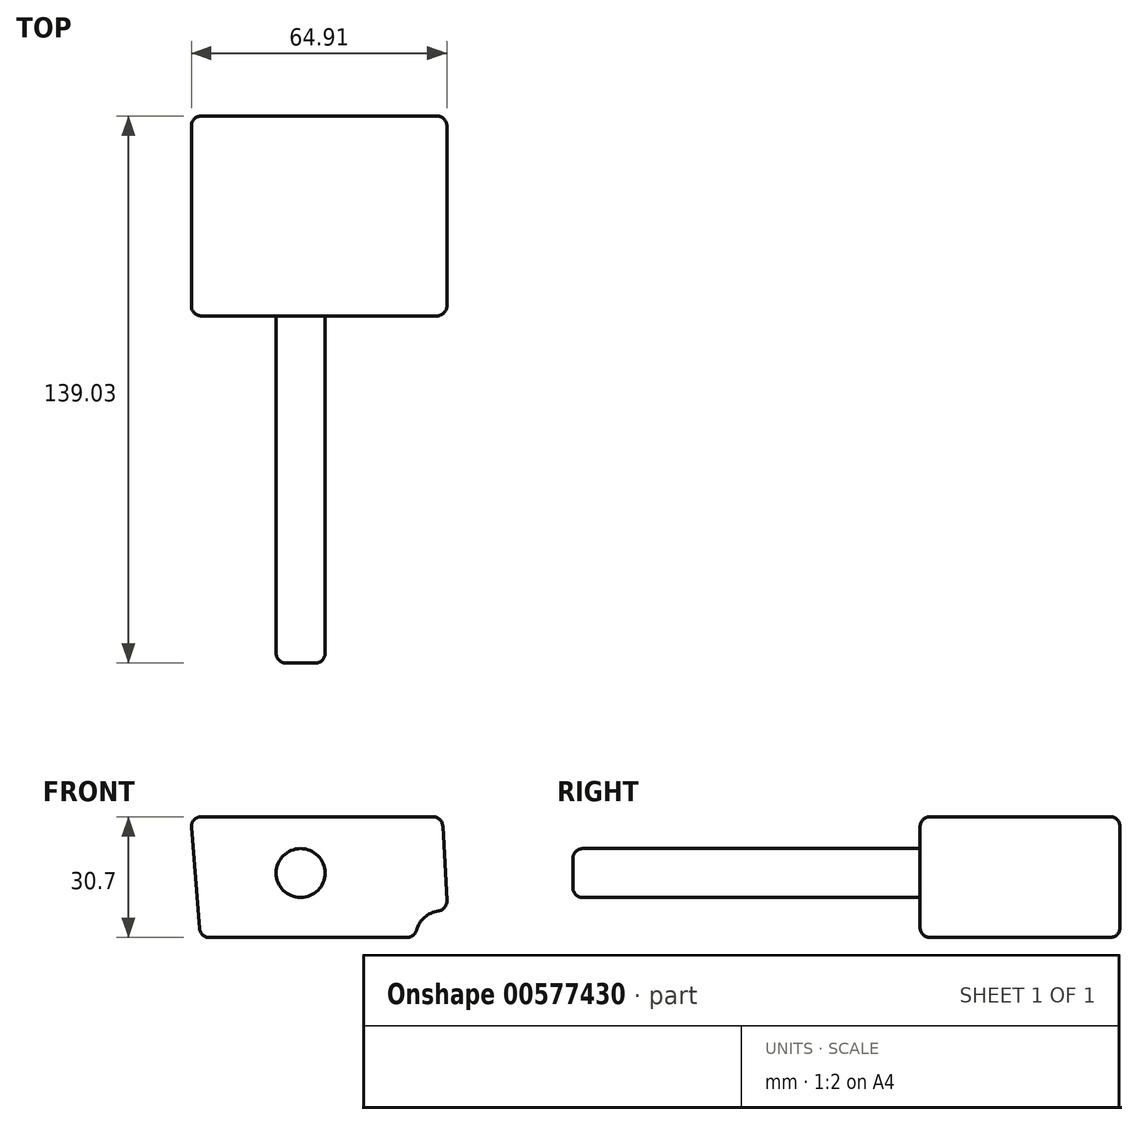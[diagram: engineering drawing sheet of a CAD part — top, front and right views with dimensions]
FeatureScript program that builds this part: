
annotation { "Feature Type Name" : "Feature", "Feature Type Description" : "" }
export const myFeature = defineFeature(function(context is Context, id is Id, definition is map)
    precondition{}
    {
        {
            var Q0;
            Q0=qCreatedBy(makeId("Front.planeOp"),FACE);
            var sketch = newSketch(context, id + "F0", { "sketchPlane" : qUnion([Q0])});
            skLineSegment(sketch, "E0", {"start": v(0, 0) * mm, "end": v(-63.97, 0) * mm});
            skLineSegment(sketch, "E1", {"start": v(-63.97, 0) * mm, "end": v(-61.53, -30.7) * mm});
            skLineSegment(sketch, "E2", {"start": v(-61.53, -30.7) * mm, "end": v(-6.83, -30.7) * mm});
            skLineSegment(sketch, "E3", {"start": v(1.3, -24) * mm, "end": v(0, 0) * mm});
            skArc(sketch, "E4", {"start": v(1.3, -24) * mm, "mid": v(-4.35, -25.44) * mm, "end": v(-6.83, -30.7) * mm});
            skSolve(sketch);
        }
        {
            var Q0;
            Q0=makeQuery(id+"F0.imprint","IMPRINT",FACE,{"disambiguationData":[TD([[makeQuery(id+"F0.imprint","IMPRINT",EDGE,{"derivedFrom":sQuery(id+"F0.wireOp",EDGE,"E0")}),1.0]])]});
            extrude(context, id + "F1", {"entities" : qUnion([Q0]), "depth" : 50.8 * mm, "offsetDistance" : 25.4 * mm});
        }
        {
            var Q0;
            Q0=makeQuery(id+"F1.opExtrude","CAP_FACE",FACE,{"disambiguationData":[OSD([sQuery(id+"F0.wireOp",EDGE,"E0"),sQuery(id+"F0.wireOp",EDGE,"E1"),sQuery(id+"F0.wireOp",EDGE,"E2"),sQuery(id+"F0.wireOp",EDGE,"9686c144-42a7-4e15-a98d-a6f16b45faf9"),sQuery(id+"F0.wireOp",EDGE,"E3")])],"isStart":false});
            var sketch = newSketch(context, id + "F2", { "sketchPlane" : qUnion([Q0])});
            skCircle(sketch, "E5", {"center": v(-36, -14.32) * mm, "radius": 6.22 * mm});
            skSolve(sketch);
        }
        {
            var Q0;
            Q0 = qSketchRegion(id + "F2", true);
            extrude(context, id + "F3", {"entities" : qUnion([Q0]), "operationType" : NewBodyOperationType.ADD, "endBound" : BoundingType.THROUGH_ALL, "depth" : 25.4 * mm, "offsetDistance" : 25.4 * mm});
        }
        {
            var Q0;
            Q0=makeQuery(id+"F3.opExtrude","CAP_EDGE",EDGE,{"disambiguationData":[OSD([sQuery(id+"F2.wireOp",EDGE,"E5")])],"isStart":false});
            var Q1;
            Q1=makeQuery(id+"F1.opExtrude","SWEPT_EDGE",EDGE,{"disambiguationData":[OSD([sQuery(id+"F0.wireOp",EDGE,"E1"),sQuery(id+"F0.wireOp",EDGE,"E2")])]});
            var Q2;
            Q2=makeQuery(id+"F1.opExtrude","SWEPT_EDGE",EDGE,{"disambiguationData":[OSD([sQuery(id+"F0.wireOp",EDGE,"E0"),sQuery(id+"F0.wireOp",EDGE,"E1")])]});
            var Q3;
            Q3=makeQuery(id+"F1.opExtrude","SWEPT_EDGE",EDGE,{"disambiguationData":[OSD([sQuery(id+"F0.wireOp",EDGE,"E3"),sQuery(id+"F0.wireOp",EDGE,"E4")])]});
            var Q4;
            Q4=makeQuery(id+"F1.opExtrude","SWEPT_EDGE",EDGE,{"disambiguationData":[OSD([sQuery(id+"F0.wireOp",EDGE,"E2"),sQuery(id+"F0.wireOp",EDGE,"E4")])]});
            var Q5;
            Q5=makeQuery(id+"F1.opExtrude","SWEPT_EDGE",EDGE,{"disambiguationData":[OSD([sQuery(id+"F0.wireOp",EDGE,"E0"),sQuery(id+"F0.wireOp",EDGE,"E3")])]});
            var Q6;
            Q6=makeQuery(id+"F1.opExtrude","CAP_EDGE",EDGE,{"disambiguationData":[OSD([sQuery(id+"F0.wireOp",EDGE,"E0")])],"isStart":true});
            var Q7;
            Q7=makeQuery(id+"F1.opExtrude","CAP_EDGE",EDGE,{"disambiguationData":[OSD([sQuery(id+"F0.wireOp",EDGE,"E1")])],"isStart":true});
            var Q8;
            Q8=makeQuery(id+"F1.opExtrude","CAP_EDGE",EDGE,{"disambiguationData":[OSD([sQuery(id+"F0.wireOp",EDGE,"E2")])],"isStart":true});
            var Q9;
            Q9=makeQuery(id+"F1.opExtrude","CAP_EDGE",EDGE,{"disambiguationData":[OSD([sQuery(id+"F0.wireOp",EDGE,"E4")])],"isStart":true});
            var Q10;
            Q10=makeQuery(id+"F1.opExtrude","CAP_EDGE",EDGE,{"disambiguationData":[OSD([sQuery(id+"F0.wireOp",EDGE,"E3")])],"isStart":true});
            var Q11;
            Q11=makeQuery(id+"F1.opExtrude","CAP_EDGE",EDGE,{"disambiguationData":[OSD([sQuery(id+"F0.wireOp",EDGE,"E0")])],"isStart":false});
            var Q12;
            Q12=makeQuery(id+"F1.opExtrude","CAP_EDGE",EDGE,{"disambiguationData":[OSD([sQuery(id+"F0.wireOp",EDGE,"E3")])],"isStart":false});
            var Q13;
            Q13=makeQuery(id+"F1.opExtrude","CAP_EDGE",EDGE,{"disambiguationData":[OSD([sQuery(id+"F0.wireOp",EDGE,"E4")])],"isStart":false});
            var Q14;
            Q14=makeQuery(id+"F1.opExtrude","CAP_EDGE",EDGE,{"disambiguationData":[OSD([sQuery(id+"F0.wireOp",EDGE,"E2")])],"isStart":false});
            var Q15;
            Q15=makeQuery(id+"F1.opExtrude","CAP_EDGE",EDGE,{"disambiguationData":[OSD([sQuery(id+"F0.wireOp",EDGE,"E1")])],"isStart":false});
            var Q16;
            Q16=makeQuery(id+"F3.opExtrude","CAP_EDGE",EDGE,{"disambiguationData":[OSD([sQuery(id+"F2.wireOp",EDGE,"E5")])],"isStart":true});
            fillet(context, id + "F4", {"entities" : qUnion([Q0, Q1, Q2, Q3, Q4, Q5, Q6, Q7, Q8, Q9, Q10, Q11, Q12, Q13, Q14, Q15, Q16]), "radius" : 2.54 * mm, "tangentPropagation" : true, "allowEdgeOverflow" : false});
        }
    });
